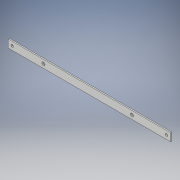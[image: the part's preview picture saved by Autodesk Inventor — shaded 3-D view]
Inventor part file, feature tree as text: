
AUTODESK INVENTOR PART (.ipt)
format: ipt  version: 2018 (Build 220112000, 112)  size: 118,784 bytes
history: native  units: in
note: dims shown in document units (in); Inventor stores cm internally (conversion verified against a paired STEP export)
features: extrude x2, sketch x2
ambient origin geometry x8: Origin, YZ Plane, XZ Plane, XY Plane, X Axis, Y Axis, Z Axis, Center Point
bodies: Solid1 (feature_tree)
feature tree (4):
  extrude  "Extrusion1"  Depth=4.949in
  extrude  "Extrusion2"  Depth=0.0394in
  sketch  "Sketch1"  dims[d0=0.2362in d1=4.949in]
  sketch  "Sketch2"  dims[d2=0.0394in d3=0.0in d4=1.1752in d5=1.0768in d6=0.0984in d7=0.0984in d8=0.25in d9=0.25in d10=0.125in d11=0.125in d12=0.0787in d13=0.0787in d14=1.0in d15=0.0in]
